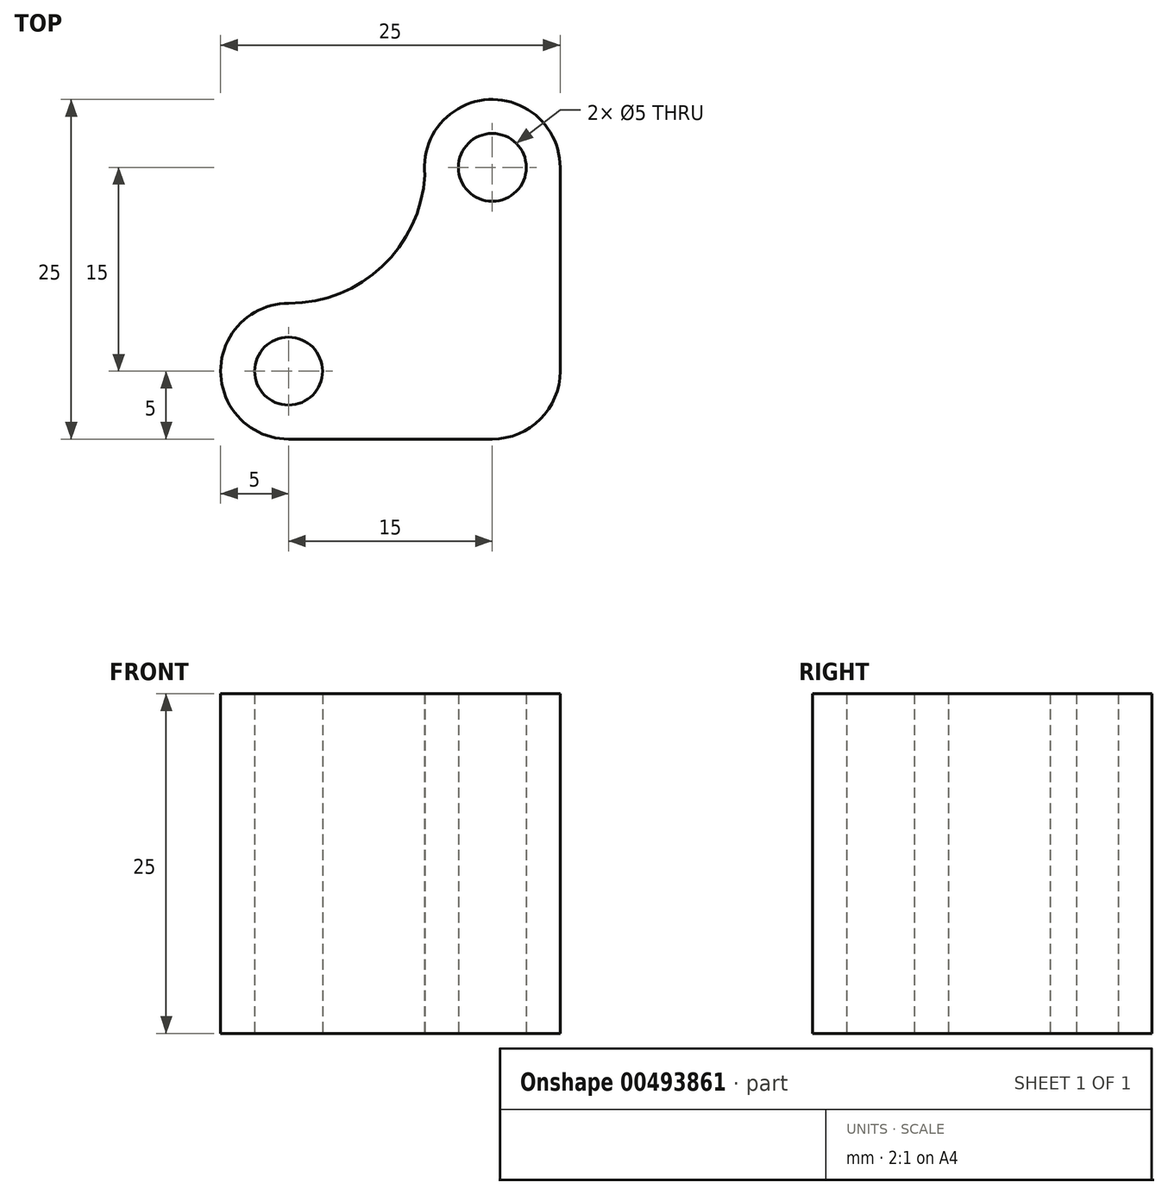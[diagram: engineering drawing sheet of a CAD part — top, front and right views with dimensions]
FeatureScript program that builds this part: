
annotation { "Feature Type Name" : "Feature", "Feature Type Description" : "" }
export const myFeature = defineFeature(function(context is Context, id is Id, definition is map)
    precondition{}
    {
        {
            var Q0;
            Q0=qCreatedBy(makeId("Top.planeOp"),FACE);
            var sketch = newSketch(context, id + "F0", { "sketchPlane" : qUnion([Q0])});
            skCircle(sketch, "E0", {"center": v(0, 15) * mm, "radius": 2.5 * mm});
            skArc(sketch, "E1", {"start": v(5, 15) * mm, "mid": v(-0.28, 20) * mm, "end": v(-4.97, 14.45) * mm});
            skLineSegment(sketch, "E2", {"start": v(5, 15) * mm, "end": v(5, 0) * mm});
            skArc(sketch, "E3", {"start": v(0, -5) * mm, "mid": v(3.54, -3.54) * mm, "end": v(5, 0) * mm});
            skCircle(sketch, "E4", {"center": v(-15, 0) * mm, "radius": 2.5 * mm});
            skArc(sketch, "E5", {"start": v(-14.98, 5) * mm, "mid": v(-20, 0) * mm, "end": v(-15, -5) * mm});
            skArc(sketch, "E6", {"start": v(-14.98, 5) * mm, "mid": v(-8.1, 7.73) * mm, "end": v(-4.97, 14.45) * mm});
            skLineSegment(sketch, "E7", {"start": v(0, -5) * mm, "end": v(-15, -5) * mm});
            skSolve(sketch);
        }
        {
            var Q0;
            Q0=makeQuery(id+"F0.imprint","IMPRINT",FACE,{"disambiguationData":[TD([[makeQuery(id+"F0.imprint","IMPRINT",EDGE,{"derivedFrom":sQuery(id+"F0.wireOp",EDGE,"E0")}),-1.0]])]});
            extrude(context, id + "F1", {"entities" : qUnion([Q0]), "depth" : 25 * mm});
        }
    });
